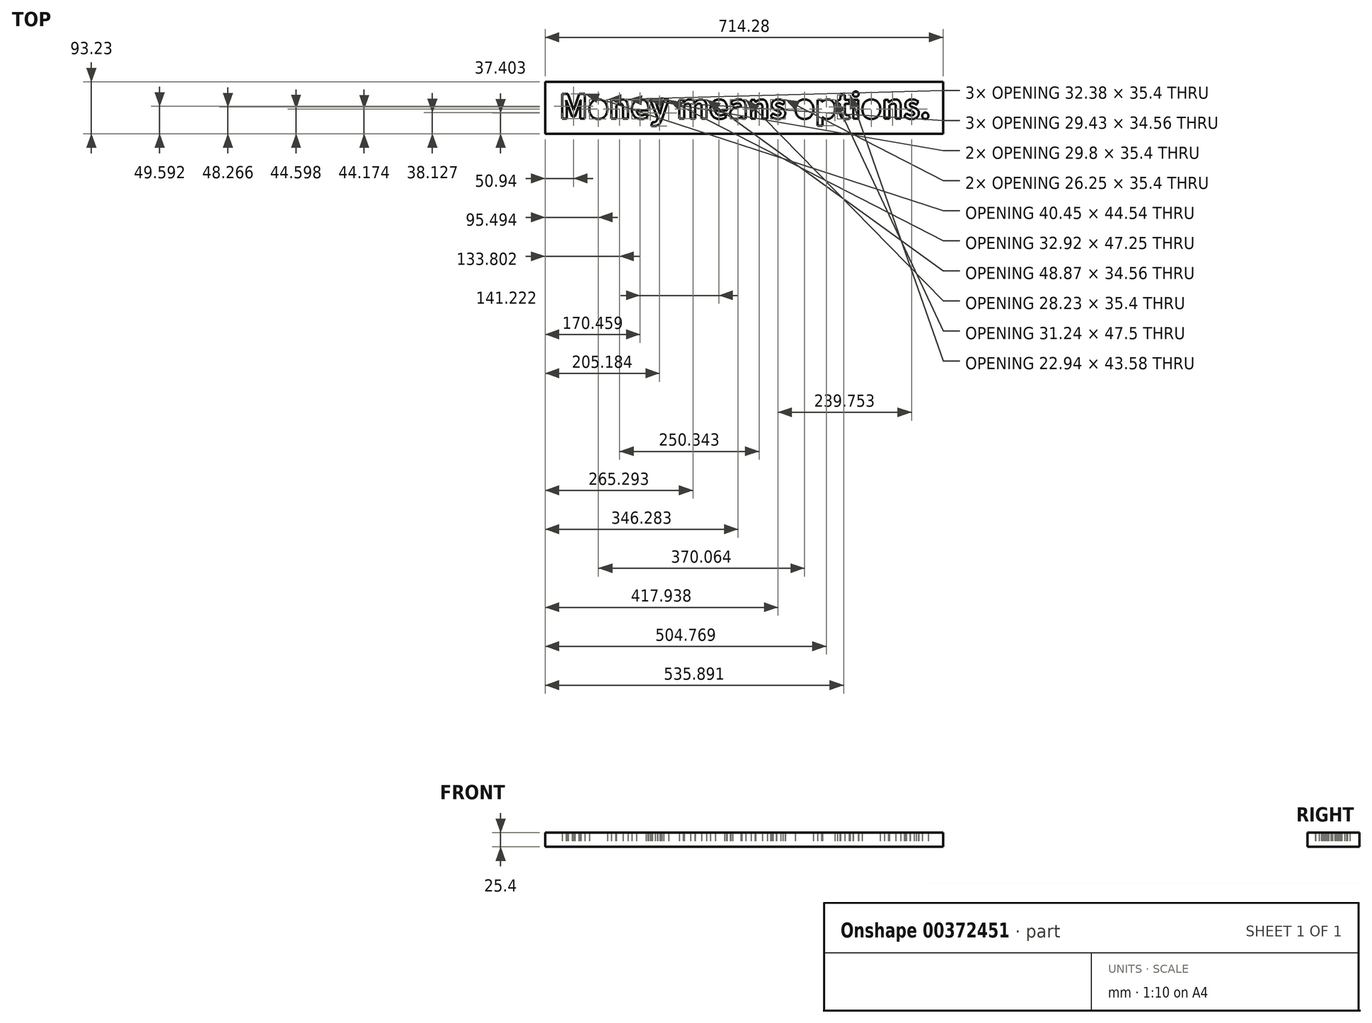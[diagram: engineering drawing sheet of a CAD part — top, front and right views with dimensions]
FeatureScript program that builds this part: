
annotation { "Feature Type Name" : "Feature", "Feature Type Description" : "" }
export const myFeature = defineFeature(function(context is Context, id is Id, definition is map)
    precondition{}
    {
        {
            var Q0;
            Q0=qCreatedBy(makeId("Top.planeOp"),FACE);
            var sketch = newSketch(context, id + "F0", { "sketchPlane" : qUnion([Q0])});
            skText(sketch, "E0", { "text": "Money means options.", "fontName": "NotoSansCJKsc-Bold.otf"});
            skLineSegment(sketch, "E1.bottom", {"start": v(-208.12, -27.32) * mm, "end": v(506.16, -27.32) * mm});
            skLineSegment(sketch, "E1.top", {"start": v(-208.12, 65.91) * mm, "end": v(506.16, 65.91) * mm});
            skLineSegment(sketch, "E1.left", {"start": v(-208.12, -27.32) * mm, "end": v(-208.12, 65.91) * mm});
            skLineSegment(sketch, "E1.right", {"start": v(506.16, -27.32) * mm, "end": v(506.16, 65.91) * mm});
            const initialGuessF0  = {"E0": [-0.18288, 0, 1, 0, 0.04334]};
            skSetInitialGuess(sketch, initialGuessF0);
            skSolve(sketch);
        }
        {
            var Q0;
            Q0 = qSketchRegion(id + "F0", true);
            extrude(context, id + "F1", {"entities" : qUnion([Q0]), "depth" : 25.4 * mm});
        }
    });
